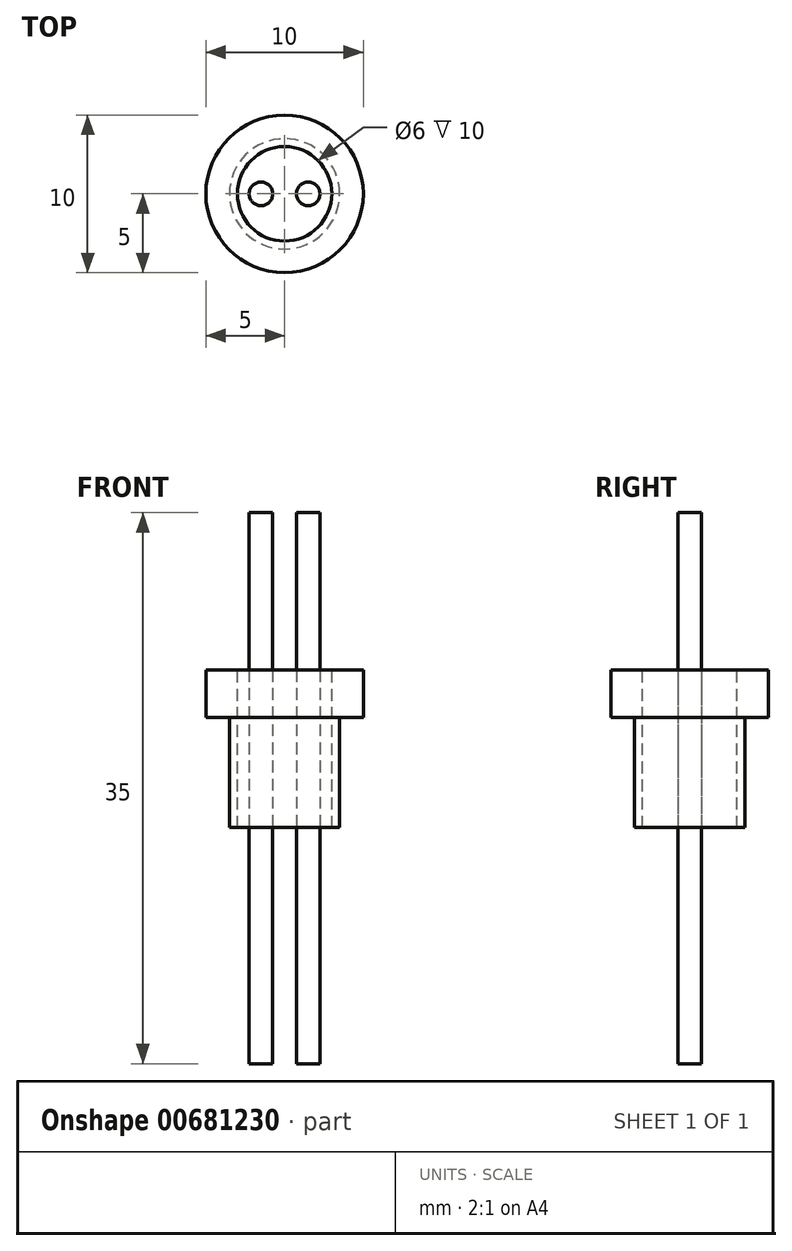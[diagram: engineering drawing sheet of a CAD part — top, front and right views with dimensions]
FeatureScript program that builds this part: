
annotation { "Feature Type Name" : "Feature", "Feature Type Description" : "" }
export const myFeature = defineFeature(function(context is Context, id is Id, definition is map)
    precondition{}
    {
        {
            var Q0;
            Q0=qCreatedBy(makeId("Top.planeOp"),FACE);
            var sketch = newSketch(context, id + "F0", { "sketchPlane" : qUnion([Q0])});
            skCircle(sketch, "E0", {"center": v(0, 0) * mm, "radius": 3.5 * mm});
            skSolve(sketch);
        }
        {
            var Q0;
            Q0 = qSketchRegion(id + "F0", true);
            extrude(context, id + "F1", {"entities" : qUnion([Q0]), "depth" : 10 * mm, "offsetDistance" : 25.4 * mm});
        }
        {
            var Q0;
            Q0=makeQuery(id+"F1.opExtrude","CAP_FACE",FACE,{"disambiguationData":[OSD([sQuery(id+"F0.wireOp",EDGE,"E0")])],"isStart":false});
            var sketch = newSketch(context, id + "F2", { "sketchPlane" : qUnion([Q0])});
            skCircle(sketch, "E1", {"center": v(0, 0) * mm, "radius": 5 * mm});
            skSolve(sketch);
        }
        {
            var Q0;
            Q0 = qSketchRegion(id + "F2", true);
            extrude(context, id + "F3", {"entities" : qUnion([Q0]), "operationType" : NewBodyOperationType.ADD, "oppositeDirection" : true, "depth" : 3 * mm, "offsetDistance" : 25 * mm});
        }
        {
            var Q0;
            Q0=makeQuery(id+"F3.boolean.opBoolean","MERGE",FACE,{"derivedFrom":[makeQuery(id+"F1.opExtrude","CAP_FACE",FACE,{"disambiguationData":[OSD([sQuery(id+"F0.wireOp",EDGE,"E0")])],"isStart":false}),makeQuery(id+"F3.opExtrude","CAP_FACE",FACE,{"disambiguationData":[OSD([sQuery(id+"F2.wireOp",EDGE,"E1")])],"isStart":true})]});
            var sketch = newSketch(context, id + "F4", { "sketchPlane" : qUnion([Q0])});
            skCircle(sketch, "E2", {"center": v(0, 0) * mm, "radius": 3 * mm});
            skSolve(sketch);
        }
        {
            var Q0;
            Q0 = qSketchRegion(id + "F4", true);
            extrude(context, id + "F5", {"entities" : qUnion([Q0]), "operationType" : NewBodyOperationType.REMOVE, "oppositeDirection" : true, "depth" : 25 * mm, "offsetDistance" : 25 * mm});
        }
        {
            var Q0;
            Q0 = qSketchRegion(id + "F4", true);
            extrude(context, id + "F6", {"entities" : qUnion([Q0]), "oppositeDirection" : true, "depth" : 10 * mm, "offsetDistance" : 25 * mm});
        }
        {
            var Q0;
            Q0=makeQuery(id+"F6.opExtrude","CAP_FACE",FACE,{"disambiguationData":[OSD([sQuery(id+"F4.wireOp",EDGE,"E2")])],"isStart":true});
            var sketch = newSketch(context, id + "F7", { "sketchPlane" : qUnion([Q0])});
            skCircle(sketch, "E3", {"center": v(-1.5, 0) * mm, "radius": 0.75 * mm});
            skCircle(sketch, "E4.MirrorC", {"center": v(1.5, 0) * mm, "radius": 0.75 * mm});
            skSolve(sketch);
        }
        {
            var Q0;
            Q0 = qSketchRegion(id + "F7", true);
            extrude(context, id + "F8", {"entities" : qUnion([Q0]), "depth" : 10 * mm, "offsetDistance" : 25 * mm, "hasSecondDirection" : true, "secondDirectionOppositeDirection" : true, "secondDirectionDepth" : 25 * mm});
        }
    });
